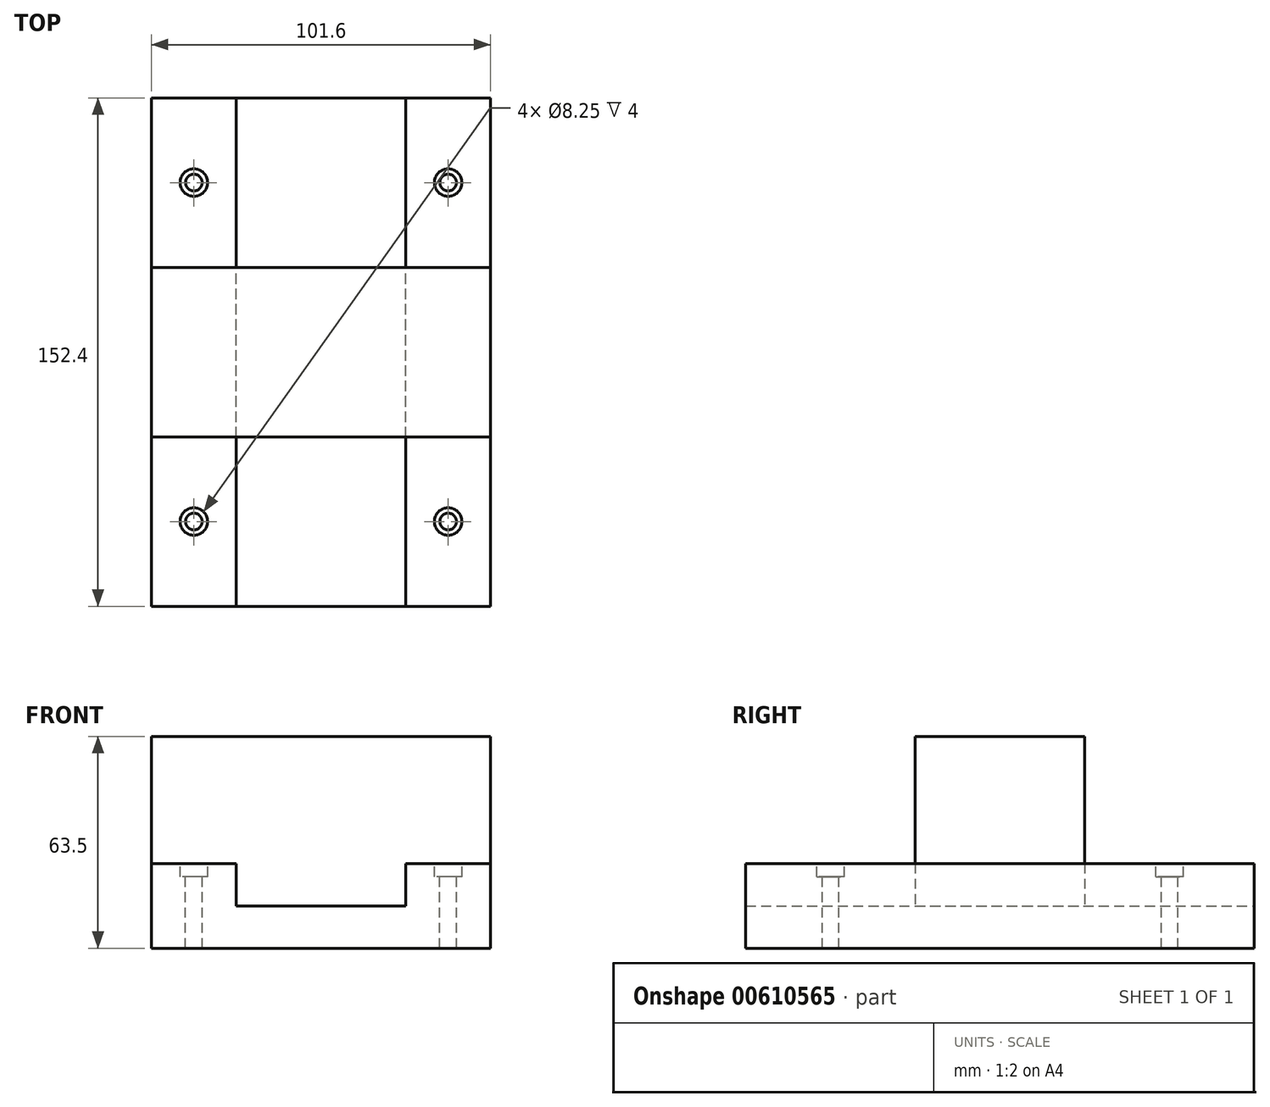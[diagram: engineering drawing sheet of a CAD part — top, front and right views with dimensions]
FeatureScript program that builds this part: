
annotation { "Feature Type Name" : "Feature", "Feature Type Description" : "" }
export const myFeature = defineFeature(function(context is Context, id is Id, definition is map)
    precondition{}
    {
        {
            var Q0;
            Q0=qCreatedBy(makeId("Front.planeOp"),FACE);
            var sketch = newSketch(context, id + "F0", { "sketchPlane" : qUnion([Q0])});
            skLineSegment(sketch, "E0.right", {"start": v(50.8, 25.4) * mm, "end": v(50.8, 0) * mm});
            skLineSegment(sketch, "E1.top", {"start": v(0, 12.7) * mm, "end": v(25.4, 12.7) * mm});
            skLineSegment(sketch, "E1.right", {"start": v(25.4, 25.4) * mm, "end": v(25.4, 12.7) * mm});
            skLineSegment(sketch, "E2.trimOffspring", {"start": v(25.4, 25.4) * mm, "end": v(50.8, 25.4) * mm});
            skLineSegment(sketch, "E3", {"start": v(0, 0) * mm, "end": v(50.8, 0) * mm});
            skLineSegment(sketch, "E4", {"start": v(0, 0) * mm, "end": v(0, 12.7) * mm, "construction": true});
            skLineSegment(sketch, "E5.MirrorCS", {"start": v(0, 12.7) * mm, "end": v(-25.4, 12.7) * mm});
            skLineSegment(sketch, "E6.MirrorCS", {"start": v(-25.4, 25.4) * mm, "end": v(-25.4, 12.7) * mm});
            skLineSegment(sketch, "E7.MirrorCS", {"start": v(-25.4, 25.4) * mm, "end": v(-50.8, 25.4) * mm});
            skLineSegment(sketch, "E8.MirrorCS", {"start": v(-50.8, 25.4) * mm, "end": v(-50.8, 0) * mm});
            skLineSegment(sketch, "E9.MirrorCS", {"start": v(0, 0) * mm, "end": v(-50.8, 0) * mm});
            skSolve(sketch);
        }
        {
            var Q0;
            Q0=makeQuery(id+"F0.imprint","IMPRINT",FACE,{"disambiguationData":[TD([[makeQuery(id+"F0.imprint","IMPRINT",EDGE,{"derivedFrom":sQuery(id+"F0.wireOp",EDGE,"E0.right")}),-1.0]])]});
            extrude(context, id + "F1", {"entities" : qUnion([Q0]), "endBound" : BoundingType.SYMMETRIC, "depth" : 152.4 * mm, "offsetDistance" : 25.4 * mm});
        }
        {
            var Q0;
            Q0=qCreatedBy(makeId("Front.planeOp"),FACE);
            var sketch = newSketch(context, id + "F2", { "sketchPlane" : qUnion([Q0])});
            skPoint(sketch, "E10.0", {"position": v(-25.4, 19.05) * mm});
            skLineSegment(sketch, "E11.0", {"start": v(-25.4, 12.7) * mm, "end": v(25.4, 12.7) * mm});
            skPoint(sketch, "E12.0", {"position": v(25.4, 19.05) * mm});
            skLineSegment(sketch, "E13.0", {"start": v(25.4, 25.4) * mm, "end": v(25.4, 12.7) * mm});
            skLineSegment(sketch, "E14.0", {"start": v(-25.4, 25.4) * mm, "end": v(-25.4, 12.7) * mm});
            skLineSegment(sketch, "E15.0", {"start": v(-25.4, 25.4) * mm, "end": v(-50.8, 25.4) * mm});
            skLineSegment(sketch, "E16.0", {"start": v(25.4, 25.4) * mm, "end": v(50.8, 25.4) * mm});
            skLineSegment(sketch, "E17", {"start": v(-50.8, 25.4) * mm, "end": v(-50.8, 63.5) * mm});
            skLineSegment(sketch, "E18", {"start": v(-50.8, 63.5) * mm, "end": v(50.8, 63.5) * mm});
            skLineSegment(sketch, "E19", {"start": v(50.8, 63.5) * mm, "end": v(50.8, 25.4) * mm});
            skSolve(sketch);
        }
        {
            var Q0;
            Q0=makeQuery(id+"F2.imprint","IMPRINT",FACE,{"disambiguationData":[TD([[makeQuery(id+"F2.imprint","IMPRINT",EDGE,{"derivedFrom":sQuery(id+"F2.wireOp",EDGE,"E11.0")}),1.0]])]});
            extrude(context, id + "F3", {"entities" : qUnion([Q0]), "endBound" : BoundingType.SYMMETRIC, "depth" : 50.8 * mm, "offsetDistance" : 25.4 * mm});
        }
        {
            var Q0;
            Q0=makeQuery(id+"F1.opExtrude","SWEPT_FACE",FACE,{"disambiguationData":[OSD([sQuery(id+"F0.wireOp",EDGE,"E2.trimOffspring")])]});
            var sketch = newSketch(context, id + "F4", { "sketchPlane" : qUnion([Q0])});
            skLineSegment(sketch, "E20.bottom", {"start": v(38.1, 50.8) * mm, "end": v(-38.1, 50.8) * mm, "construction": true});
            skLineSegment(sketch, "E20.top", {"start": v(38.1, -50.8) * mm, "end": v(-38.1, -50.8) * mm, "construction": true});
            skLineSegment(sketch, "E20.left", {"start": v(38.1, 50.8) * mm, "end": v(38.1, -50.8) * mm, "construction": true});
            skLineSegment(sketch, "E20.right", {"start": v(-38.1, 50.8) * mm, "end": v(-38.1, -50.8) * mm, "construction": true});
            skPoint(sketch, "E20.middle", {"position": v(0, 0) * mm});
            skSolve(sketch);
        }
        {
            var Q0;
            Q0=sQuery(id+"F4.wireOp",VERTEX,"E20.right.start");
            var Q1;
            Q1=sQuery(id+"F4.wireOp",VERTEX,"E20.bottom.start");
            var Q2;
            Q2=sQuery(id+"F4.wireOp",VERTEX,"E20.left.end");
            var Q3;
            Q3=sQuery(id+"F4.wireOp",VERTEX,"E20.right.end");
            var Q4;
            Q4=makeQuery(id+"F1.opExtrude","SWEPT_BODY",BODY,{"disambiguationData":[OSD([sQuery(id+"F0.wireOp",EDGE,"E0.right"),sQuery(id+"F0.wireOp",EDGE,"E1.top"),sQuery(id+"F0.wireOp",EDGE,"E1.right"),sQuery(id+"F0.wireOp",EDGE,"E2.trimOffspring"),sQuery(id+"F0.wireOp",EDGE,"E3"),sQuery(id+"F0.wireOp",EDGE,"E5.MirrorCS"),sQuery(id+"F0.wireOp",EDGE,"E6.MirrorCS"),sQuery(id+"F0.wireOp",EDGE,"E7.MirrorCS"),sQuery(id+"F0.wireOp",EDGE,"E8.MirrorCS"),sQuery(id+"F0.wireOp",EDGE,"E9.MirrorCS")])]});
            hole(context, id + "F5", {"style" : HoleStyle.C_BORE, "endStyle" : HoleEndStyle.THROUGH, "standardTappedOrClearance" : lookupTablePath({ "standard" : "ISO", "size" : "5", "type" : "Drilled" }), "standardBlindInLast" : lookupTablePath({ "standard" : "ISO", "size" : "5", "type" : "Drilled" }), "holeDiameter" : 5 * mm, "cBoreDiameter" : 8.25 * mm, "cBoreDepth" : 4 * mm, "majorDiameter" : 4 * mm, "isTappedThrough" : true, "tappedDepth" : 12.7 * mm, "tapClearance" : 3, "locations" : qUnion([Q0, Q1, Q2, Q3]), "scope" : qUnion([Q4])});
        }
    });
